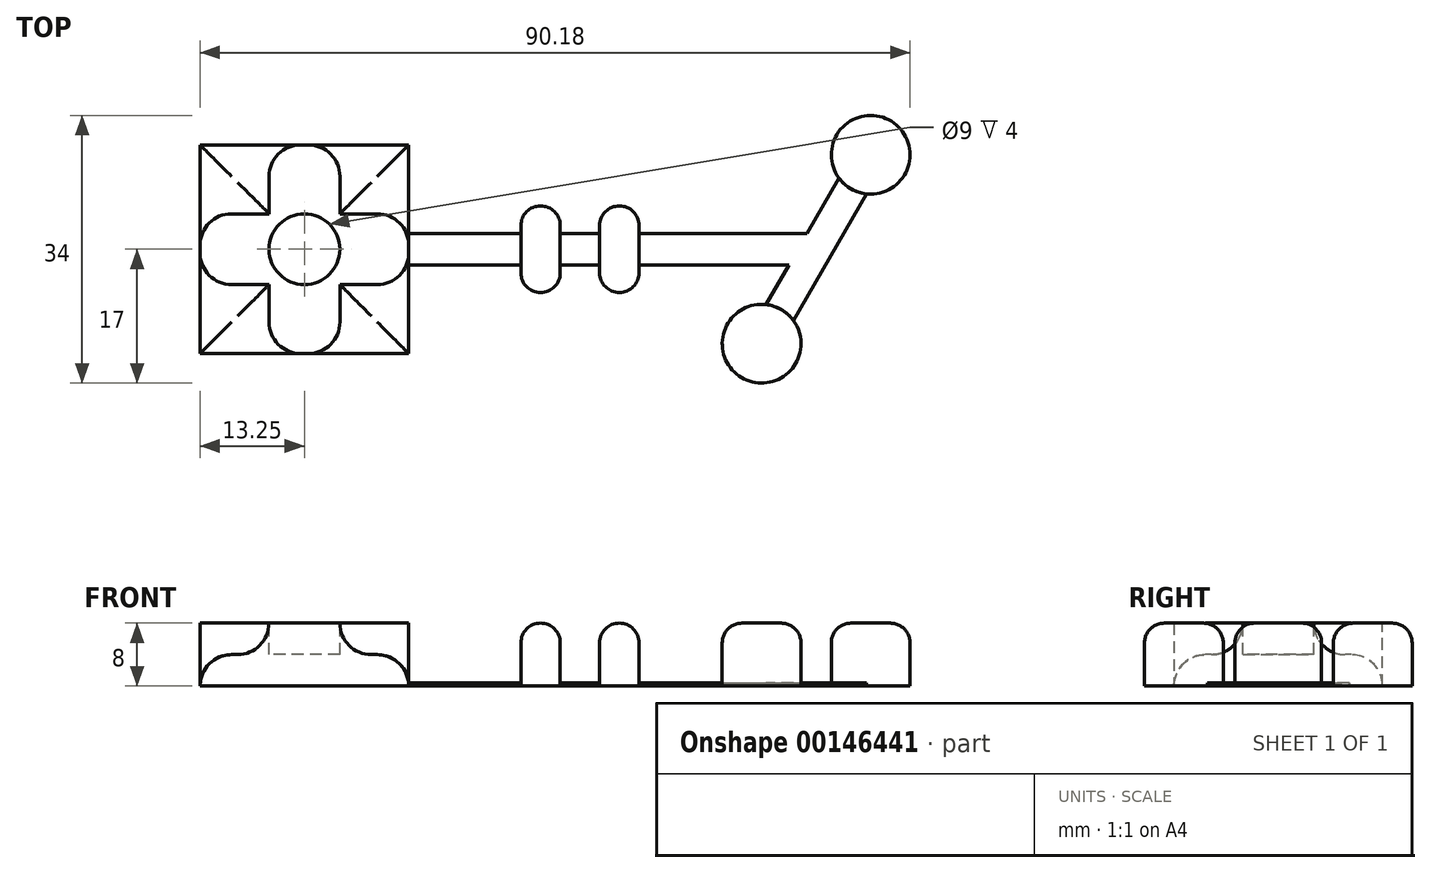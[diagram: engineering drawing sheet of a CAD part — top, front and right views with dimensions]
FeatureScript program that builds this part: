
annotation { "Feature Type Name" : "Feature", "Feature Type Description" : "" }
export const myFeature = defineFeature(function(context is Context, id is Id, definition is map)
    precondition{}
    {
        {
            var Q0;
            Q0=qCreatedBy(makeId("Top.planeOp"),FACE);
            var sketch = newSketch(context, id + "F0", { "sketchPlane" : qUnion([Q0])});
            skLineSegment(sketch, "E0.bottom", {"start": v(13.25, 13.25) * mm, "end": v(-13.25, 13.25) * mm});
            skLineSegment(sketch, "E0.top", {"start": v(13.25, -13.25) * mm, "end": v(-13.25, -13.25) * mm});
            skLineSegment(sketch, "E0.left", {"start": v(13.25, 13.25) * mm, "end": v(13.25, -13.25) * mm});
            skLineSegment(sketch, "E0.right", {"start": v(-13.25, 13.25) * mm, "end": v(-13.25, -13.25) * mm});
            skPoint(sketch, "E0.middle", {"position": v(0, 0) * mm});
            skLineSegment(sketch, "E1", {"start": v(0, 0) * mm, "end": v(65, 0) * mm, "construction": true});
            skLineSegment(sketch, "E2", {"start": v(58.13, -11.9) * mm, "end": v(71.93, 12) * mm, "construction": true});
            skPoint(sketch, "E3", {"position": v(58.07, -12) * mm});
            skCircle(sketch, "E4", {"center": v(71.93, 12) * mm, "radius": 5 * mm});
            skCircle(sketch, "E5", {"center": v(58.07, -12) * mm, "radius": 5 * mm});
            skLineSegment(sketch, "E6.bottom", {"start": v(27.5, 3) * mm, "end": v(32.5, 3) * mm});
            skLineSegment(sketch, "E6.top", {"start": v(27.5, -3) * mm, "end": v(32.5, -3) * mm});
            skLineSegment(sketch, "E6.left", {"start": v(27.5, 3) * mm, "end": v(27.5, -3) * mm});
            skLineSegment(sketch, "E6.right", {"start": v(32.5, 3) * mm, "end": v(32.5, -3) * mm});
            skPoint(sketch, "E6.middle", {"position": v(30, 0) * mm});
            skPoint(sketch, "E7.middle", {"position": v(40, 0) * mm});
            skLineSegment(sketch, "E8.bottom", {"start": v(42.5, 3) * mm, "end": v(37.5, 3) * mm});
            skLineSegment(sketch, "E8.top", {"start": v(42.5, -3) * mm, "end": v(37.5, -3) * mm});
            skLineSegment(sketch, "E8.left", {"start": v(42.5, 3) * mm, "end": v(42.5, -3) * mm});
            skLineSegment(sketch, "E8.right", {"start": v(37.5, 3) * mm, "end": v(37.5, -3) * mm});
            skArc(sketch, "E9", {"start": v(32.5, 3) * mm, "mid": v(30, 5.5) * mm, "end": v(27.5, 3) * mm});
            skArc(sketch, "E10", {"start": v(27.5, -3) * mm, "mid": v(30, -5.5) * mm, "end": v(32.5, -3) * mm});
            skArc(sketch, "E11", {"start": v(42.5, 3) * mm, "mid": v(40, 5.5) * mm, "end": v(37.5, 3) * mm});
            skArc(sketch, "E12", {"start": v(37.5, -3) * mm, "mid": v(40, -5.5) * mm, "end": v(42.5, -3) * mm});
            skLineSegment(sketch, "E13.0", {"start": v(62.1, -9.03) * mm, "end": v(71.37, 7.03) * mm});
            skLineSegment(sketch, "E14.MirrorCS", {"start": v(58.63, -7.03) * mm, "end": v(67.9, 9.03) * mm});
            skLineSegment(sketch, "E15", {"start": v(13.25, 2) * mm, "end": v(27.5, 2) * mm});
            skLineSegment(sketch, "E16", {"start": v(32.5, 2) * mm, "end": v(37.5, 2) * mm});
            skLineSegment(sketch, "E17", {"start": v(42.5, 2) * mm, "end": v(63.85, 2) * mm});
            skLineSegment(sketch, "E18.MirrorCS", {"start": v(13.25, -2) * mm, "end": v(27.5, -2) * mm});
            skLineSegment(sketch, "E19.MirrorCS", {"start": v(32.5, -2) * mm, "end": v(37.5, -2) * mm});
            skLineSegment(sketch, "E20.MirrorCS", {"start": v(42.5, -2) * mm, "end": v(61.54, -2) * mm});
            skSolve(sketch);
        }
        {
            var Q0;
            {var subQ3=sQuery(id+"F0.wireOp",EDGE,"E0.bottom");Q0=makeQuery(id+"F0.imprint","IMPRINT",FACE,{"disambiguationData":[TD([[makeQuery(id+"F0.imprint","IMPRINT",EDGE,{"derivedFrom":subQ3}),1.0]])]});}
            var Q1;
            {var subQ8=sQuery(id+"F0.wireOp",EDGE,"E6.bottom");Q1=makeQuery(id+"F0.imprint","IMPRINT",FACE,{"disambiguationData":[TD([[makeQuery(id+"F0.imprint","IMPRINT",EDGE,{"derivedFrom":subQ8}),-1.0]])]});}
            var Q2;
            Q2=makeQuery(id+"F0.imprint","IMPRINT",FACE,{"disambiguationData":[TD([[makeQuery(id+"F0.imprint","IMPRINT",EDGE,{"derivedFrom":sQuery(id+"F0.wireOp",EDGE,"E6.bottom")}),1.0]])]});
            var Q3;
            Q3=makeQuery(id+"F0.imprint","IMPRINT",FACE,{"disambiguationData":[TD([[makeQuery(id+"F0.imprint","IMPRINT",EDGE,{"derivedFrom":sQuery(id+"F0.wireOp",EDGE,"E6.top")}),-1.0]])]});
            var Q4;
            Q4=makeQuery(id+"F0.imprint","IMPRINT",FACE,{"disambiguationData":[TD([[makeQuery(id+"F0.imprint","IMPRINT",EDGE,{"derivedFrom":sQuery(id+"F0.wireOp",EDGE,"E8.bottom")}),-1.0]])]});
            var Q5;
            {var subQ4=sQuery(id+"F0.wireOp",EDGE,"E8.bottom");Q5=makeQuery(id+"F0.imprint","IMPRINT",FACE,{"disambiguationData":[TD([[makeQuery(id+"F0.imprint","IMPRINT",EDGE,{"derivedFrom":subQ4}),1.0]])]});}
            var Q6;
            Q6=makeQuery(id+"F0.imprint","IMPRINT",FACE,{"disambiguationData":[TD([[makeQuery(id+"F0.imprint","IMPRINT",EDGE,{"derivedFrom":sQuery(id+"F0.wireOp",EDGE,"E8.top")}),1.0]])]});
            var Q7;
            {var subQ0=sQuery(id+"F0.wireOp",EDGE,"E5");var subQ1=makeQuery(id+"F0.imprint","INTERSECT",VERTEX,{"derivedFrom":[subQ0,sQuery(id+"F0.wireOp",EDGE,"E13.0")]});Q7=makeQuery(id+"F0.imprint","IMPRINT",FACE,{"disambiguationData":[TD([[makeQuery(id+"F0.imprint","IMPRINT",EDGE,{"disambiguationData":[TD([[subQ1,-1.0]])],"derivedFrom":subQ0}),1.0]])]});}
            var Q8;
            {var subQ0=sQuery(id+"F0.wireOp",EDGE,"E4");var subQ1=makeQuery(id+"F0.imprint","INTERSECT",VERTEX,{"derivedFrom":[subQ0,sQuery(id+"F0.wireOp",EDGE,"E13.0")]});Q8=makeQuery(id+"F0.imprint","IMPRINT",FACE,{"disambiguationData":[TD([[makeQuery(id+"F0.imprint","IMPRINT",EDGE,{"disambiguationData":[TD([[subQ1,1.0]])],"derivedFrom":subQ0}),1.0]])]});}
            extrude(context, id + "F1", {"entities" : qUnion([Q0, Q1, Q2, Q3, Q4, Q5, Q6, Q7, Q8]), "depth" : 8 * mm});
        }
        {
            var Q0;
            {var subQ0=sQuery(id+"F0.wireOp",EDGE,"E15");Q0=makeQuery(id+"F0.imprint","IMPRINT",FACE,{"disambiguationData":[TD([[makeQuery(id+"F0.imprint","IMPRINT",EDGE,{"derivedFrom":subQ0}),-1.0]])]});}
            var Q1;
            {var subQ0=sQuery(id+"F0.wireOp",EDGE,"E16");Q1=makeQuery(id+"F0.imprint","IMPRINT",FACE,{"disambiguationData":[TD([[makeQuery(id+"F0.imprint","IMPRINT",EDGE,{"derivedFrom":subQ0}),-1.0]])]});}
            var Q2;
            {var subQ0=sQuery(id+"F0.wireOp",EDGE,"E17");Q2=makeQuery(id+"F0.imprint","IMPRINT",FACE,{"disambiguationData":[TD([[makeQuery(id+"F0.imprint","IMPRINT",EDGE,{"derivedFrom":subQ0}),-1.0]])]});}
            var Q3;
            {var subQ4=sQuery(id+"F0.wireOp",EDGE,"E13.0");Q3=makeQuery(id+"F0.imprint","IMPRINT",FACE,{"disambiguationData":[TD([[makeQuery(id+"F0.imprint","IMPRINT",EDGE,{"derivedFrom":subQ4}),1.0]])]});}
            extrude(context, id + "F2", {"entities" : qUnion([Q0, Q1, Q2, Q3]), "operationType" : NewBodyOperationType.ADD, "depth" : 0.4 * mm});
        }
        {
            var Q0;
            Q0=makeQuery(id+"F1.opExtrude","CAP_EDGE",EDGE,{"disambiguationData":[OSD([sQuery(id+"F0.wireOp",EDGE,"E5")])],"isStart":false});
            var Q1;
            Q1=makeQuery(id+"F1.opExtrude","CAP_EDGE",EDGE,{"disambiguationData":[OSD([sQuery(id+"F0.wireOp",EDGE,"E4")])],"isStart":false});
            var Q2;
            Q2=makeQuery(id+"F1.opExtrude","CAP_EDGE",EDGE,{"disambiguationData":[OSD([sQuery(id+"F0.wireOp",EDGE,"E8.left")])],"isStart":false});
            var Q3;
            Q3=makeQuery(id+"F1.opExtrude","CAP_FACE",FACE,{"disambiguationData":[OSD([sQuery(id+"F0.wireOp",EDGE,"E6.left"),sQuery(id+"F0.wireOp",EDGE,"E6.right"),sQuery(id+"F0.wireOp",EDGE,"E9"),sQuery(id+"F0.wireOp",EDGE,"E10")])],"isStart":false});
            fillet(context, id + "F3", {"entities" : qUnion([Q0, Q1, Q2, Q3]), "radius" : 2.5 * mm, "tangentPropagation" : true, "allowEdgeOverflow" : false});
        }
        {
            var Q0;
            Q0=makeQuery(id+"F1.opExtrude","CAP_FACE",FACE,{"disambiguationData":[OSD([sQuery(id+"F0.wireOp",EDGE,"E0.bottom"),sQuery(id+"F0.wireOp",EDGE,"E0.top"),sQuery(id+"F0.wireOp",EDGE,"E0.left"),sQuery(id+"F0.wireOp",EDGE,"E0.right")])],"isStart":false});
            var sketch = newSketch(context, id + "F4", { "sketchPlane" : qUnion([Q0])});
            skCircle(sketch, "E21", {"center": v(0, 0) * mm, "radius": 4.5 * mm});
            skLineSegment(sketch, "E22", {"start": v(-4.5, 13.25) * mm, "end": v(-4.5, 4.5) * mm});
            skLineSegment(sketch, "E23", {"start": v(-13.25, 4.5) * mm, "end": v(-4.5, 4.5) * mm});
            skLineSegment(sketch, "E24", {"start": v(4.5, 13.25) * mm, "end": v(4.5, 4.5) * mm});
            skLineSegment(sketch, "E25", {"start": v(-13.25, -4.5) * mm, "end": v(-4.5, -4.5) * mm});
            skLineSegment(sketch, "E26.trimOffspring", {"start": v(-4.5, -4.5) * mm, "end": v(-4.5, -13.25) * mm});
            skLineSegment(sketch, "E27.trimOffspring", {"start": v(4.5, 4.5) * mm, "end": v(13.25, 4.5) * mm});
            skLineSegment(sketch, "E28.trimOffspring", {"start": v(4.5, -4.5) * mm, "end": v(4.5, -13.25) * mm});
            skLineSegment(sketch, "E29.trimOffspring", {"start": v(4.5, -4.5) * mm, "end": v(13.25, -4.5) * mm});
            skSolve(sketch);
        }
        {
            var Q0;
            Q0=makeQuery(id+"F4.imprint","IMPRINT",FACE,{"disambiguationData":[TD([[makeQuery(id+"F4.imprint","IMPRINT",EDGE,{"derivedFrom":sQuery(id+"F4.wireOp",EDGE,"E21")}),1.0]])]});
            var Q1;
            {var subQ0=sQuery(id+"F4.wireOp",EDGE,"E24");Q1=makeQuery(id+"F4.imprint","IMPRINT",FACE,{"disambiguationData":[TD([[makeQuery(id+"F4.imprint","IMPRINT",EDGE,{"derivedFrom":subQ0}),1.0]])]});}
            var Q2;
            {var subQ0=sQuery(id+"F4.wireOp",EDGE,"E22");Q2=makeQuery(id+"F4.imprint","IMPRINT",FACE,{"disambiguationData":[TD([[makeQuery(id+"F4.imprint","IMPRINT",EDGE,{"derivedFrom":subQ0}),-1.0]])]});}
            var Q3;
            {var subQ0=sQuery(id+"F4.wireOp",EDGE,"E25");Q3=makeQuery(id+"F4.imprint","IMPRINT",FACE,{"disambiguationData":[TD([[makeQuery(id+"F4.imprint","IMPRINT",EDGE,{"derivedFrom":subQ0}),-1.0]])]});}
            var Q4;
            {var subQ0=sQuery(id+"F4.wireOp",EDGE,"E28.trimOffspring");Q4=makeQuery(id+"F4.imprint","IMPRINT",FACE,{"disambiguationData":[TD([[makeQuery(id+"F4.imprint","IMPRINT",EDGE,{"derivedFrom":subQ0}),1.0]])]});}
            extrude(context, id + "F5", {"entities" : qUnion([Q0, Q1, Q2, Q3, Q4]), "operationType" : NewBodyOperationType.REMOVE, "oppositeDirection" : true, "depth" : 4 * mm});
        }
        {
            var Q0;
            Q0=makeQuery(id+"F5.boolean.opBoolean","COPY",FACE,{"derivedFrom":makeQuery(id+"F5.opExtrude","CAP_FACE",FACE,{"disambiguationData":[OSD([sQuery(id+"F0.wireOp",EDGE,"E0.bottom"),sQuery(id+"F0.wireOp",EDGE,"E0.right"),sQuery(id+"F4.wireOp",EDGE,"E22"),sQuery(id+"F4.wireOp",EDGE,"E23")])],"isStart":false})});
            var Q1;
            {var subQ0=sQuery(id+"F0.wireOp",EDGE,"E0.left");var subQ1=makeQuery(id+"F1.opExtrude","CAP_EDGE",EDGE,{"disambiguationData":[OSD([subQ0])],"isStart":false});Q1=makeQuery(id+"F5.boolean.opBoolean","COPY",EDGE,{"derivedFrom":makeQuery(id+"F5.opExtrude","CAP_EDGE",EDGE,{"disambiguationData":[OSD([subQ0]),TDD([makeQuery(id+"F4.imprint","IMPRINT",EDGE,{"disambiguationData":[TD([[makeQuery(id+"F4.imprint","INTERSECT",VERTEX,{"derivedFrom":[makeQuery(id+"F1.opExtrude","CAP_EDGE",EDGE,{"disambiguationData":[OSD([sQuery(id+"F0.wireOp",EDGE,"E0.bottom")])],"isStart":false}),subQ1]}),-1.0]])],"derivedFrom":subQ1})])],"isStart":false})});}
            var Q2;
            Q2=makeQuery(id+"F5.boolean.opBoolean","COPY",FACE,{"derivedFrom":makeQuery(id+"F5.opExtrude","CAP_FACE",FACE,{"disambiguationData":[OSD([sQuery(id+"F0.wireOp",EDGE,"E0.bottom"),sQuery(id+"F0.wireOp",EDGE,"E0.left"),sQuery(id+"F4.wireOp",EDGE,"E24"),sQuery(id+"F4.wireOp",EDGE,"E27.trimOffspring")])],"isStart":false})});
            var Q3;
            Q3=makeQuery(id+"F5.boolean.opBoolean","COPY",FACE,{"derivedFrom":makeQuery(id+"F5.opExtrude","CAP_FACE",FACE,{"disambiguationData":[OSD([sQuery(id+"F0.wireOp",EDGE,"E0.top"),sQuery(id+"F0.wireOp",EDGE,"E0.right"),sQuery(id+"F4.wireOp",EDGE,"E25"),sQuery(id+"F4.wireOp",EDGE,"E26.trimOffspring")])],"isStart":false})});
            var Q4;
            Q4=makeQuery(id+"F5.boolean.opBoolean","COPY",FACE,{"derivedFrom":makeQuery(id+"F5.opExtrude","CAP_FACE",FACE,{"disambiguationData":[OSD([sQuery(id+"F0.wireOp",EDGE,"E0.top"),sQuery(id+"F0.wireOp",EDGE,"E0.left"),sQuery(id+"F4.wireOp",EDGE,"E28.trimOffspring"),sQuery(id+"F4.wireOp",EDGE,"E29.trimOffspring")])],"isStart":false})});
            fillet(context, id + "F6", {"entities" : qUnion([Q0, Q1, Q2, Q3, Q4]), "radius" : 4 * mm, "tangentPropagation" : true, "allowEdgeOverflow" : false});
        }
    });
